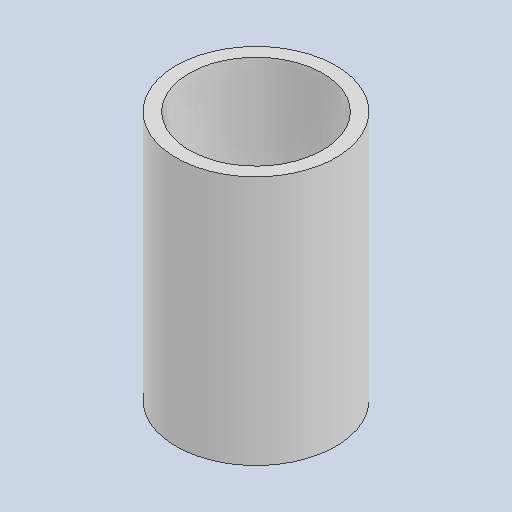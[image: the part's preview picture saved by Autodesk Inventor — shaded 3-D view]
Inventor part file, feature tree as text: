
AUTODESK INVENTOR PART (.ipt)
format: ipt  version: 2025.2 (Build 292293000, 293)  size: 91,648 bytes
history: native  units: in
note: dims shown in document units (in); Inventor stores cm internally (conversion verified against a paired STEP export)
features: extrude x1, sketch x1
ambient origin geometry x8: Origin, YZ Plane, XZ Plane, XY Plane, X Axis, Y Axis, Z Axis, Center Point
bodies: Solid1 (feature_tree)
feature tree (2):
  extrude  "Extrusion1"  Depth=0.313in
  sketch  "Sketch1"  dims[d0=0.2in d1=0.167in d2=0.313in d3=0.0in]
